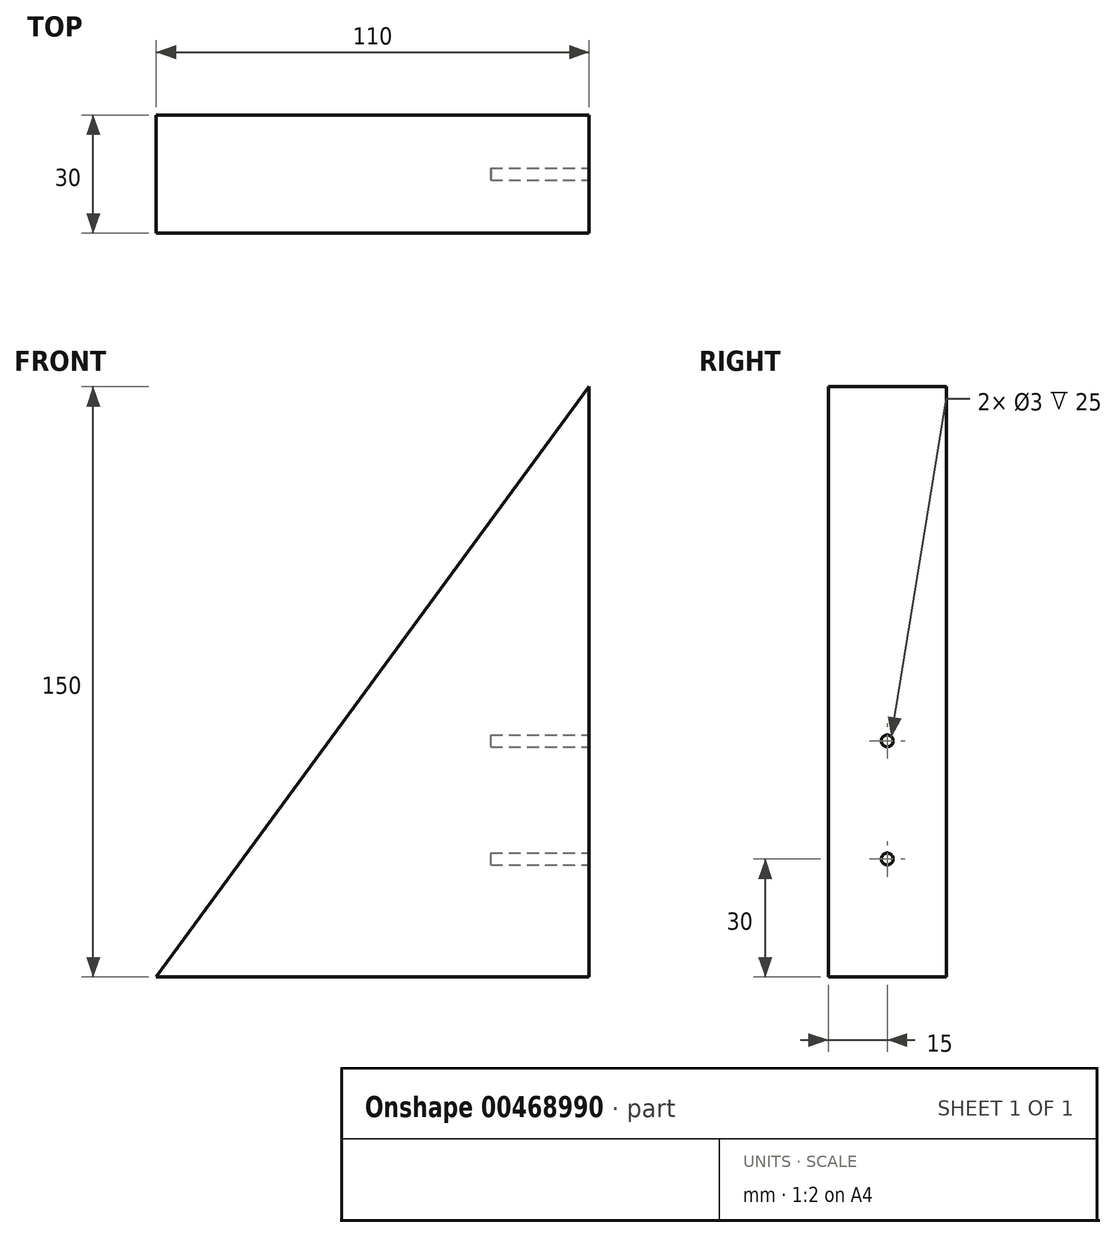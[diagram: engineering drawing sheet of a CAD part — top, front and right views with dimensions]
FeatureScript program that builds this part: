
annotation { "Feature Type Name" : "Feature", "Feature Type Description" : "" }
export const myFeature = defineFeature(function(context is Context, id is Id, definition is map)
    precondition{}
    {
        {
            var Q0;
            Q0=qCreatedBy(makeId("Front.planeOp"),FACE);
            var sketch = newSketch(context, id + "F0", { "sketchPlane" : qUnion([Q0])});
            skLineSegment(sketch, "E0.bottom", {"start": v(0, 0) * mm, "end": v(110, 0) * mm});
            skLineSegment(sketch, "E0.right", {"start": v(110, 0) * mm, "end": v(110, 150) * mm});
            skLineSegment(sketch, "E1", {"start": v(110, 150) * mm, "end": v(0, 0) * mm});
            skSolve(sketch);
        }
        {
            var Q0;
            Q0 = qSketchRegion(id + "F0", true);
            var Q1;
            Q1 = qSketchRegion(id + "Fzu9LDZ0IwX8nAT_0", true);
            extrude(context, id + "F1", {"entities" : qUnion([Q0, Q1]), "depth" : 30 * mm});
        }
        {
            var Q0;
            Q0=makeQuery(id+"F1.opExtrude","SWEPT_FACE",FACE,{"disambiguationData":[OSD([sQuery(id+"F0.wireOp",EDGE,"E0.right")])]});
            var sketch = newSketch(context, id + "F2", { "sketchPlane" : qUnion([Q0])});
            skCircle(sketch, "E2", {"center": v(-15, 30) * mm, "radius": 1.5 * mm});
            skPoint(sketch, "E2.centerSnap0", {"position": v(-15, 0) * mm});
            skCircle(sketch, "E3", {"center": v(-15, 60) * mm, "radius": 1.5 * mm});
            skSolve(sketch);
        }
        {
            var Q0;
            Q0 = qSketchRegion(id + "F2", true);
            extrude(context, id + "F3", {"entities" : qUnion([Q0]), "operationType" : NewBodyOperationType.REMOVE, "oppositeDirection" : true, "depth" : 25 * mm});
        }
    });
